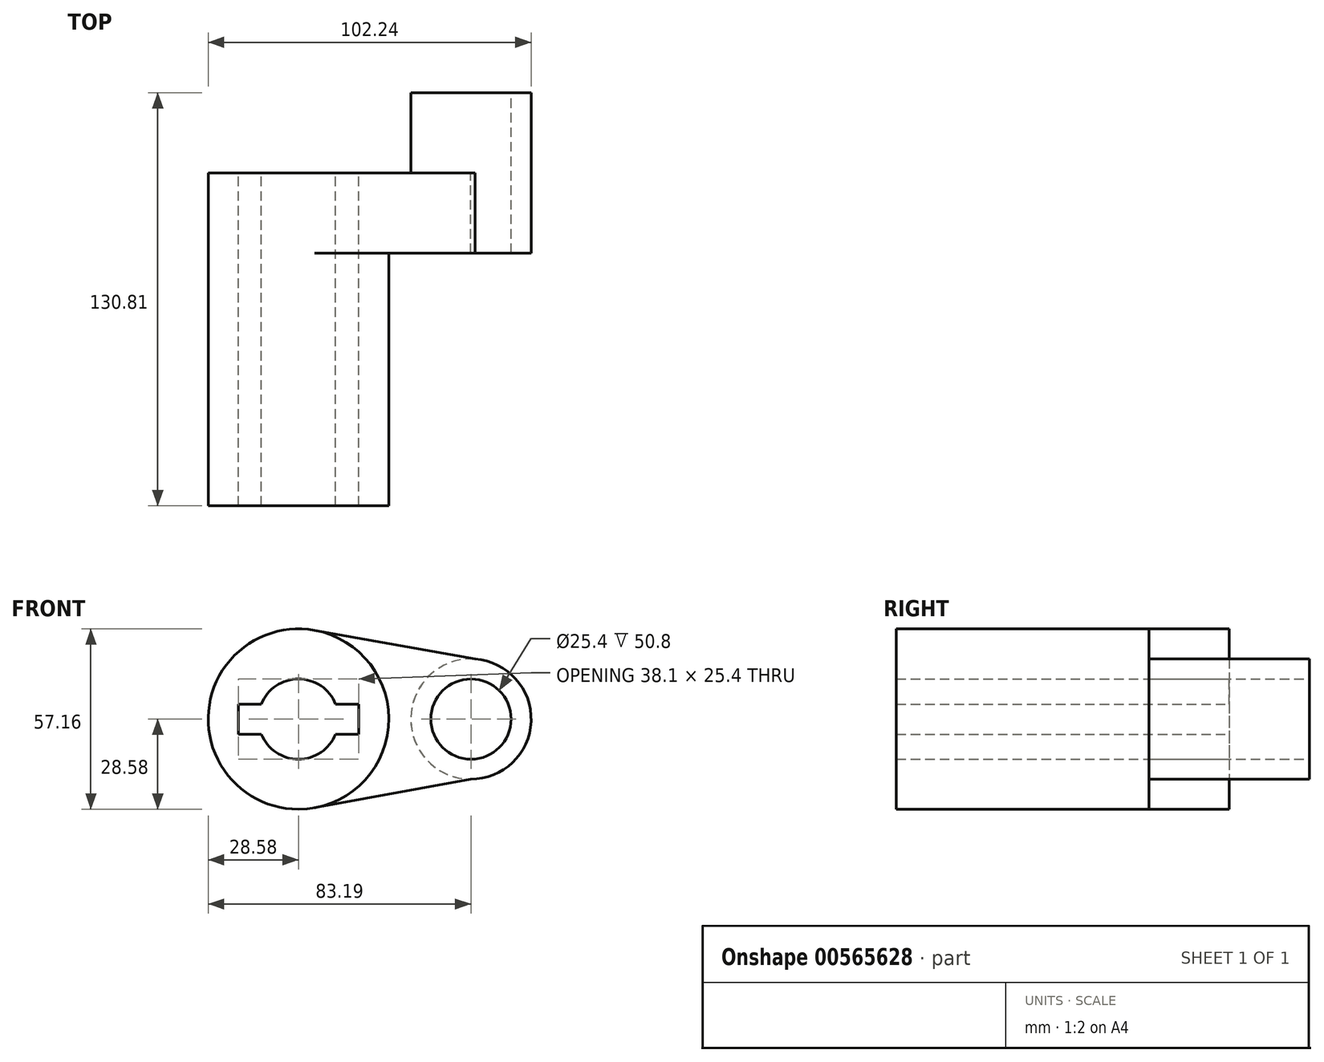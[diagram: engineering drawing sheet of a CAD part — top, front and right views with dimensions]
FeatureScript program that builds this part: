
annotation { "Feature Type Name" : "Feature", "Feature Type Description" : "" }
export const myFeature = defineFeature(function(context is Context, id is Id, definition is map)
    precondition{}
    {
        {
            var Q0;
            Q0=qCreatedBy(makeId("Front.planeOp"),FACE);
            var sketch = newSketch(context, id + "F0", { "sketchPlane" : qUnion([Q0])});
            skCircle(sketch, "E0", {"center": v(0, 0) * mm, "radius": 28.57 * mm});
            skCircle(sketch, "E1", {"center": v(54.61, 0) * mm, "radius": 19.05 * mm});
            skLineSegment(sketch, "E2", {"start": v(5.04, 28.13) * mm, "end": v(55.9, 19) * mm});
            skLineSegment(sketch, "E3", {"start": v(5.16, -28.1) * mm, "end": v(54.46, -19.05) * mm});
            skCircle(sketch, "E4", {"center": v(0, 0) * mm, "radius": 12.7 * mm});
            skCircle(sketch, "E5", {"center": v(54.61, 0) * mm, "radius": 12.7 * mm});
            skLineSegment(sketch, "E6.bottom", {"start": v(-19.05, 4.76) * mm, "end": v(19.05, 4.76) * mm});
            skLineSegment(sketch, "E6.top", {"start": v(-19.05, -4.76) * mm, "end": v(19.05, -4.76) * mm});
            skLineSegment(sketch, "E6.left", {"start": v(-19.05, 4.76) * mm, "end": v(-19.05, -4.76) * mm});
            skLineSegment(sketch, "E6.right", {"start": v(19.05, 4.76) * mm, "end": v(19.05, -4.76) * mm});
            skSolve(sketch);
        }
        {
            var Q0;
            Q0=makeQuery(id+"F0.imprint","IMPRINT",FACE,{"disambiguationData":[TD([[makeQuery(id+"F0.imprint","IMPRINT",EDGE,{"derivedFrom":sQuery(id+"F0.wireOp",EDGE,"E5")}),-1.0]])]});
            var Q1;
            {var subQ7=sQuery(id+"F0.wireOp",EDGE,"E6.left");Q1=makeQuery(id+"F0.imprint","IMPRINT",FACE,{"disambiguationData":[TD([[makeQuery(id+"F0.imprint","IMPRINT",EDGE,{"derivedFrom":subQ7}),-1.0]])]});}
            var Q2;
            {var subQ0=sQuery(id+"F0.wireOp",EDGE,"E2");Q2=makeQuery(id+"F0.imprint","IMPRINT",FACE,{"disambiguationData":[TD([[makeQuery(id+"F0.imprint","IMPRINT",EDGE,{"derivedFrom":subQ0}),-1.0]])]});}
            extrude(context, id + "F1", {"entities" : qUnion([Q0, Q1, Q2]), "depth" : 25.4 * mm, "offsetDistance" : 25.4 * mm});
        }
        {
            var Q0;
            {var subQ7=sQuery(id+"F0.wireOp",EDGE,"E6.left");Q0=makeQuery(id+"F0.imprint","IMPRINT",FACE,{"disambiguationData":[TD([[makeQuery(id+"F0.imprint","IMPRINT",EDGE,{"derivedFrom":subQ7}),-1.0]])]});}
            extrude(context, id + "F2", {"entities" : qUnion([Q0]), "operationType" : NewBodyOperationType.ADD, "depth" : 52.32 * mm, "offsetDistance" : 25.4 * mm});
        }
        {
            var Q0;
            Q0=makeQuery(id+"F2.opExtrude","CAP_FACE",FACE,{"disambiguationData":[OSD([sQuery(id+"F0.wireOp",EDGE,"E0"),sQuery(id+"F0.wireOp",EDGE,"E4"),sQuery(id+"F0.wireOp",EDGE,"E6.bottom"),sQuery(id+"F0.wireOp",EDGE,"E6.top"),sQuery(id+"F0.wireOp",EDGE,"E6.left"),sQuery(id+"F0.wireOp",EDGE,"E6.right")])],"isStart":false});
            extrude(context, id + "F3", {"entities" : qUnion([Q0]), "operationType" : NewBodyOperationType.ADD, "depth" : 53.1 * mm, "offsetDistance" : 25.4 * mm});
        }
        {
            var Q0;
            Q0=makeQuery(id+"F0.imprint","IMPRINT",FACE,{"disambiguationData":[TD([[makeQuery(id+"F0.imprint","IMPRINT",EDGE,{"derivedFrom":sQuery(id+"F0.wireOp",EDGE,"E5")}),-1.0]])]});
            extrude(context, id + "F4", {"entities" : qUnion([Q0]), "operationType" : NewBodyOperationType.ADD, "oppositeDirection" : true, "depth" : 25.4 * mm, "offsetDistance" : 25.4 * mm});
        }
    });
